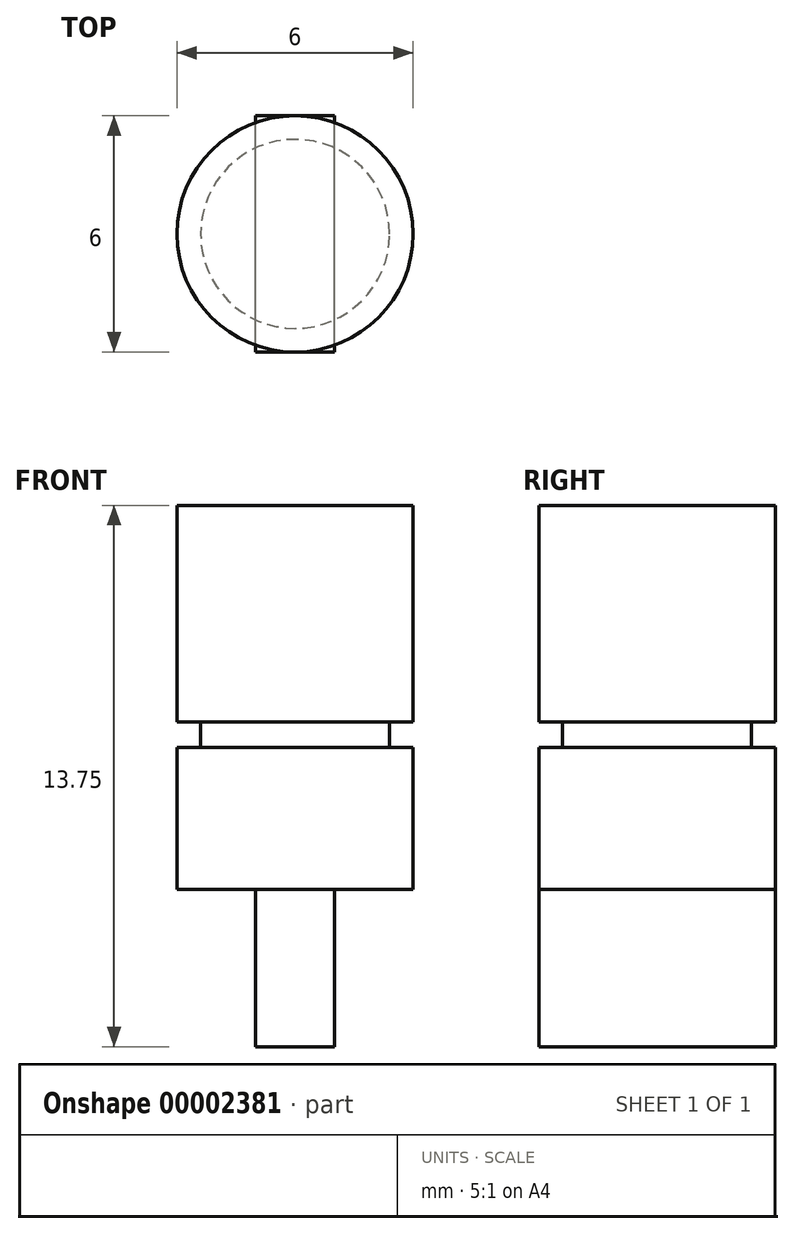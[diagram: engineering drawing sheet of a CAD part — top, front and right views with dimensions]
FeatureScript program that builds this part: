
annotation { "Feature Type Name" : "Feature", "Feature Type Description" : "" }
export const myFeature = defineFeature(function(context is Context, id is Id, definition is map)
    precondition{}
    {
        {
            var Q0;
            Q0=qCreatedBy(makeId("Front.planeOp"),FACE);
            var sketch = newSketch(context, id + "F0", { "sketchPlane" : qUnion([Q0])});
            skLineSegment(sketch, "E0", {"start": v(1, 0) * mm, "end": v(3, 0) * mm});
            skLineSegment(sketch, "E1", {"start": v(3, 0) * mm, "end": v(3, 3.6) * mm});
            skLineSegment(sketch, "E2", {"start": v(3, 3.6) * mm, "end": v(2.4, 3.6) * mm});
            skLineSegment(sketch, "E3", {"start": v(2.4, 3.6) * mm, "end": v(2.4, 4.25) * mm});
            skLineSegment(sketch, "E4", {"start": v(2.4, 4.25) * mm, "end": v(3, 4.25) * mm});
            skLineSegment(sketch, "E5", {"start": v(3, 4.25) * mm, "end": v(3, 9.75) * mm});
            skLineSegment(sketch, "E6", {"start": v(3, 9.75) * mm, "end": v(0, 9.75) * mm});
            skLineSegment(sketch, "E7", {"start": v(0, 9.75) * mm, "end": v(0, 0) * mm});
            skLineSegment(sketch, "E8", {"start": v(0, -4) * mm, "end": v(1, -4) * mm});
            skLineSegment(sketch, "E9", {"start": v(1, 0) * mm, "end": v(1, -4) * mm});
            skLineSegment(sketch, "E10", {"start": v(0, 0) * mm, "end": v(1, 0) * mm});
            skPoint(sketch, "E11", {"position": v(0, 0) * mm});
            skLineSegment(sketch, "E12", {"start": v(0, 0) * mm, "end": v(-1, 0) * mm});
            skLineSegment(sketch, "E13", {"start": v(-1, 0) * mm, "end": v(-1, -4) * mm});
            skLineSegment(sketch, "E14", {"start": v(-1, -4) * mm, "end": v(0, -4) * mm});
            skSolve(sketch);
        }
        {
            var Q0;
            Q0=makeQuery(id+"F0.imprint","IMPRINT",FACE,{"disambiguationData":[TD([[makeQuery(id+"F0.imprint","IMPRINT",EDGE,{"derivedFrom":sQuery(id+"F0.wireOp",EDGE,"E0")}),1.0]])]});
            var Q1;
            Q1=sQuery(id+"F0.wireOp",EDGE,"E7");
            revolve(context, id + "F1", {"entities" : qUnion([Q0]), "axis" : qUnion([Q1]), "revolveType" : RevolveType.FULL});
        }
        {
            var Q0;
            Q0=makeQuery(id+"F0.imprint","IMPRINT",FACE,{"disambiguationData":[TD([[makeQuery(id+"F0.imprint","IMPRINT",EDGE,{"derivedFrom":sQuery(id+"F0.wireOp",EDGE,"E9")}),-1.0]])]});
            extrude(context, id + "F2", {"entities" : qUnion([Q0]), "operationType" : NewBodyOperationType.ADD, "endBound" : BoundingType.SYMMETRIC, "depth" : 6 * mm});
        }
    });
